MODEL slx_fafc3af4f6b2
KIND model
BLOCK [Scope] Actuator Schedule
  DataFormat = StructureWithTime
  Floating = off
  LimitDataPoints = off
  NumInputPorts = 1
  Ports = [1]
  SaveName = nschedule6
  ShowLegends = off
  TimeRange = 2
  YMax = 1.1
  YMin = 0.9
BLOCK [Scope] CAN 2 Schedule
  DataFormat = StructureWithTime
  Floating = off
  LimitDataPoints = off
  NumInputPorts = 1
  Ports = [1]
  SaveName = nschedule3
  ShowLegends = off
  TimeRange = 2
  YMax = 3.5
  YMin = 1
  ZoomMode = xonly
BLOCK [Scope] CAN 3 Schedule
  DataFormat = StructureWithTime
  Floating = off
  LimitDataPoints = off
  NumInputPorts = 1
  Ports = [1]
  SaveName = nschedule5
  ShowLegends = off
  TimeRange = 2
  YMax = 3.5
  YMin = 1
  ZoomMode = xonly
BLOCK [Scope] CAN1 Schedule
  DataFormat = StructureWithTime
  Floating = off
  LimitDataPoints = off
  NumInputPorts = 1
  Ports = [1]
  SaveName = nschedule
  ShowLegends = off
  TimeRange = 2
  YMax = 3.5
  YMin = 1
  ZoomMode = xonly
BLOCK [Clock] Clock
BLOCK [Scope] Controller Schedule
  DataFormat = StructureWithTime
  Floating = off
  LimitDataPoints = off
  NumInputPorts = 1
  Ports = [1]
  SaveName = nschedule2
  ShowLegends = off
  TimeRange = 2
  YMax = 1.5
  YMin = 1
BLOCK [Demux] Demux
  DisplayOption = bar
  Outputs = 2
  Ports = [1, 2]
BLOCK [Display] Display
  Decimation = 1
  Lockdown = off
  Ports = [1]
BLOCK [Scope] End-to-end delay
  DataFormat = StructureWithTime
  Floating = off
  LimitDataPoints = off
  NumInputPorts = 1
  Ports = [1]
  SaveName = nschedule9
  ShowLegends = off
  TimeRange = 2
  YMax = 0.04
  YMin = 0
BLOCK [From] From
  GotoTag = ctrl
BLOCK [From] From1
  GotoTag = meas
BLOCK [Scope] Gateway Schedule
  DataFormat = StructureWithTime
  Floating = off
  LimitDataPoints = off
  NumInputPorts = 1
  Ports = [1]
  SaveName = nschedule4
  ShowLegends = off
  TimeRange = 2
  YMax = 1.5
  YMin = 1
BLOCK [Goto] Goto
  GotoTag = ctrl
BLOCK [Goto] Goto1
  GotoTag = meas
BLOCK [Reference] Process  REF=simulink_extras/Additional
Linear/Transfer Fcn
(with initial outputs)
  D = [10  1]
  N = [10]
  Ports = [1, 1]
  SourceBlock = simulink_extras/Additional\nLinear/Transfer Fcn\n(with initial outputs)
  SourceType = Transfer Function with Initial Outputs
  U0 = 0
  Y0 = 1
BLOCK [Scope] Process input
  DataFormat = StructureWithTime
  Floating = off
  LimitDataPoints = off
  NumInputPorts = 1
  Ports = [1]
  SaveName = nschedule8
  ShowLegends = off
  TimeRange = 2
  YMax = 1.00000
  YMin = -1.00000
BLOCK [Scope] Process output
  DataFormat = StructureWithTime
  Floating = off
  LimitDataPoints = off
  NumInputPorts = 1
  Ports = [1]
  SaveName = nschedule7
  ShowLegends = off
  TimeRange = 2
  YMax = 1
  YMin = 0
BLOCK [Scope] Sensor Schedule
  DataFormat = StructureWithTime
  Floating = off
  LimitDataPoints = off
  NumInputPorts = 1
  Ports = [1]
  SaveName = nschedule1
  ShowLegends = off
  TimeRange = 2
  YMax = 1.5
  YMin = 1
  ZoomMode = xonly
BLOCK [Reference] TrueTime Kernel (Actuator)  REF=truetime/TrueTime Kernel  (lib defined in slx_0362a698a4ec)
  Ports = [0, 2]
  Priority = 1
  SourceBlock = truetime/TrueTime Kernel
  args = []
  battery = off
  clockoffsetdrift = [0 0]
  label = 3: 1
  ninputsoutputs = [0 2]
  ntriggers = 0
  nwnodenbr = [3 1]
  poweroutput = off
  schedoutput = on
  sfun = actuator_init
  trigtype = rising
BLOCK [Reference] TrueTime Kernel (Controller)  REF=truetime/TrueTime Kernel  (lib defined in slx_0362a698a4ec)
  Ports = [0, 1]
  Priority = 1
  SourceBlock = truetime/TrueTime Kernel
  args = []
  battery = off
  clockoffsetdrift = [0 0]
  label = 2: 1
  ninputsoutputs = [0 0]
  ntriggers = 0
  nwnodenbr = [2 1]
  poweroutput = off
  schedoutput = on
  sfun = controller_init
  trigtype = rising
BLOCK [Reference] TrueTime Kernel (Gateway)  REF=truetime/TrueTime Kernel  (lib defined in slx_0362a698a4ec)
  Ports = [0, 1]
  Priority = 1
  SourceBlock = truetime/TrueTime Kernel
  args = []
  battery = off
  clockoffsetdrift = [0 0]
  label = 1: 2\n2: 2\n3: 2
  ninputsoutputs = [0 0]
  ntriggers = 0
  nwnodenbr = [1 2; 2 2; 3 2]
  poweroutput = off
  schedoutput = on
  sfun = gateway_init
  trigtype = rising
BLOCK [Reference] TrueTime Kernel (Network disturbance traffic generator)  REF=truetime/TrueTime Kernel  (lib defined in slx_0362a698a4ec)
  Ports = []
  Priority = 1
  SourceBlock = truetime/TrueTime Kernel
  args = []
  battery = off
  clockoffsetdrift = [0 0]
  label = 1: 3\n2: 3\n3: 3
  ninputsoutputs = [0 0]
  ntriggers = 0
  nwnodenbr = [1 3; 2 3; 3 3]
  poweroutput = off
  schedoutput = off
  sfun = disturbance_init
  trigtype = rising
BLOCK [Reference] TrueTime Kernel (Sensor)  REF=truetime/TrueTime Kernel  (lib defined in slx_0362a698a4ec)
  Ports = [1, 1]
  Priority = 1
  SourceBlock = truetime/TrueTime Kernel
  args = []
  battery = off
  clockoffsetdrift = [0 0]
  label = 1: 1
  ninputsoutputs = [1 0]
  ntriggers = 0
  nwnodenbr = [1 1]
  poweroutput = off
  schedoutput = on
  sfun = sensor_init
  trigtype = rising
BLOCK [Reference] TrueTime Network (CAN 1)  REF=truetime/TrueTime Network  (lib defined in slx_0362a698a4ec)
  NIT = 0
  Ports = [0, 1]
  Priority = 1
  QSortMode = FIFO
  SourceBlock = truetime/TrueTime Network
  SourceType = Real-Time Network
  bandwidths = [0.5 0.25 0.25]
  buftype = Common buffer
  dynSchedule = []
  irtSchedule = 0
  lossprob = 0
  memsize = 80000
  miniSlotSize = 40
  minsize = 29
  nnodes = 3
  nodeGraph = 0
  nrtLength = 0
  nwnbr = 1
  nwtype = CSMA/AMP (CAN)
  overflow = Retransmit
  rate = 125000
  schedule = [1 2 1 3]
  scheduleoutput = on
  seed = 0
  slotsize = 80
  sync = 0
BLOCK [Reference] TrueTime Network (CAN 2)  REF=truetime/TrueTime Network  (lib defined in slx_0362a698a4ec)
  NIT = 0
  Ports = [0, 1]
  Priority = 1
  QSortMode = FIFO
  SourceBlock = truetime/TrueTime Network
  SourceType = Real-Time Network
  bandwidths = [0.5 0.25 0.25]
  buftype = Common buffer
  dynSchedule = []
  irtSchedule = 0
  lossprob = 0
  memsize = 80000
  miniSlotSize = 40
  minsize = 29
  nnodes = 3
  nodeGraph = 0
  nrtLength = 0
  nwnbr = 2
  nwtype = CSMA/AMP (CAN)
  overflow = Retransmit
  rate = 125000
  schedule = [1 2 1 3]
  scheduleoutput = on
  seed = 0
  slotsize = 80
  sync = 0
BLOCK [Reference] TrueTime Network (CAN 3)  REF=truetime/TrueTime Network  (lib defined in slx_0362a698a4ec)
  NIT = 0
  Ports = [0, 1]
  Priority = 1
  QSortMode = FIFO
  SourceBlock = truetime/TrueTime Network
  SourceType = Real-Time Network
  bandwidths = [0.5 0.25 0.25]
  buftype = Common buffer
  dynSchedule = []
  irtSchedule = 0
  lossprob = 0
  memsize = 80000
  miniSlotSize = 40
  minsize = 29
  nnodes = 3
  nodeGraph = 0
  nrtLength = 0
  nwnbr = 3
  nwtype = CSMA/AMP (CAN)
  overflow = Retransmit
  rate = 125000
  schedule = [1 2 1 3]
  scheduleoutput = on
  seed = 0
  slotsize = 80
  sync = 0
ANNOTATION (root): TrueTime 2.0 Multi-Networked Control System with Gateway <copyright redacted>
LINE Clock:1 -> Display:1
LINE Demux:1 -> Goto:1
LINE Demux:2 -> End-to-end delay:1
LINE From1:1 -> TrueTime Kernel (Sensor):1
NET From:1 -> Process input:1, Process:1
NET Process:1 -> Goto1:1, Process output:1
LINE TrueTime Kernel (Actuator):1 -> Demux:1
LINE TrueTime Kernel (Actuator):2 -> Actuator Schedule:1
LINE TrueTime Kernel (Controller):1 -> Controller Schedule:1
LINE TrueTime Kernel (Gateway):1 -> Gateway Schedule:1
LINE TrueTime Kernel (Sensor):1 -> Sensor Schedule:1
LINE TrueTime Network (CAN 1):1 -> CAN1 Schedule:1
LINE TrueTime Network (CAN 2):1 -> CAN 2 Schedule:1
LINE TrueTime Network (CAN 3):1 -> CAN 3 Schedule:1
note: NET lines group one-source signal fan-out (src -> all destinations, sorted); 1:1 wires keep LINE
